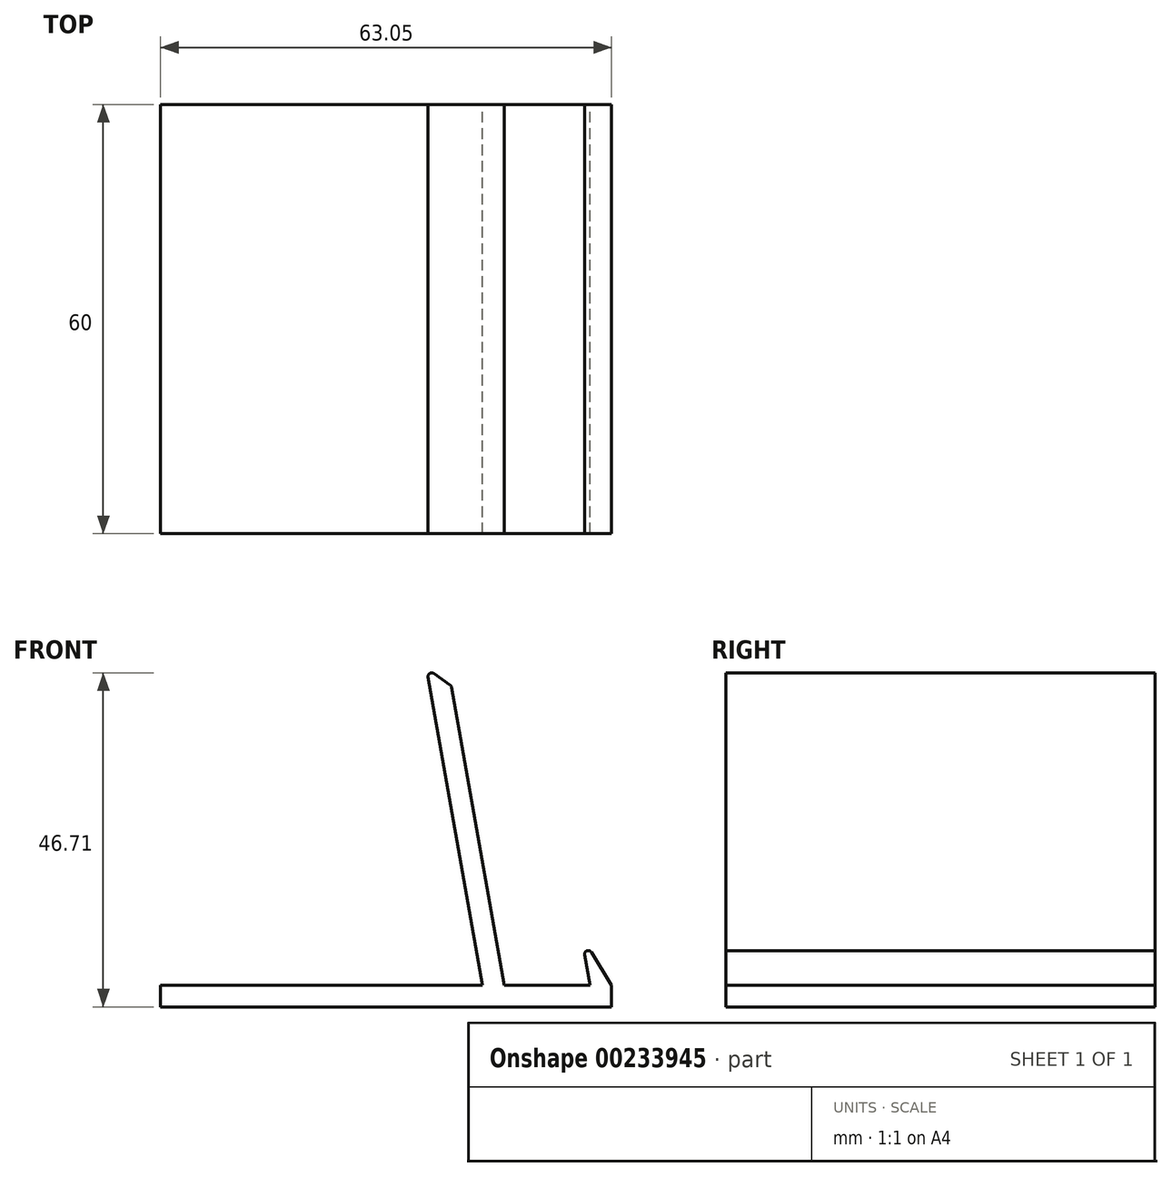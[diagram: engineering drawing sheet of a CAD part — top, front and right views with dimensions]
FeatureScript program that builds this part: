
annotation { "Feature Type Name" : "Feature", "Feature Type Description" : "" }
export const myFeature = defineFeature(function(context is Context, id is Id, definition is map)
    precondition{}
    {
        {
            var Q0;
            Q0=qCreatedBy(makeId("Front.planeOp"),FACE);
            var sketch = newSketch(context, id + "F0", { "sketchPlane" : qUnion([Q0])});
            skLineSegment(sketch, "E0", {"start": v(0, 0) * mm, "end": v(-63.05, 0) * mm});
            skLineSegment(sketch, "E1", {"start": v(-63.05, 0) * mm, "end": v(-63.05, 3) * mm});
            skLineSegment(sketch, "E2", {"start": v(-63.05, 3) * mm, "end": v(-18.05, 3) * mm});
            skLineSegment(sketch, "E3", {"start": v(-18.05, 3) * mm, "end": v(-25.86, 47.32) * mm});
            skLineSegment(sketch, "E4", {"start": v(-25.86, 47.32) * mm, "end": v(-22.39, 44.88) * mm});
            skLineSegment(sketch, "E5", {"start": v(-22.39, 44.88) * mm, "end": v(-15, 3) * mm});
            skLineSegment(sketch, "E6", {"start": v(-15, 3) * mm, "end": v(-3, 3) * mm});
            skLineSegment(sketch, "E7", {"start": v(-3, 3) * mm, "end": v(-4.22, 9.9) * mm});
            skLineSegment(sketch, "E8", {"start": v(-4.22, 9.9) * mm, "end": v(0, 3) * mm});
            skLineSegment(sketch, "E9", {"start": v(0, 3) * mm, "end": v(0, 0) * mm});
            skSolve(sketch);
        }
        {
            var Q0;
            Q0=makeQuery(id+"F0.imprint","IMPRINT",FACE,{"disambiguationData":[TD([[makeQuery(id+"F0.imprint","IMPRINT",EDGE,{"derivedFrom":sQuery(id+"F0.wireOp",EDGE,"E0")}),-1.0]])]});
            extrude(context, id + "F1", {"entities" : qUnion([Q0]), "endBound" : BoundingType.SYMMETRIC, "depth" : 60 * mm});
        }
        {
            var Q0;
            Q0=makeQuery(id+"F1.opExtrude","SWEPT_EDGE",EDGE,{"disambiguationData":[OSD([sQuery(id+"F0.wireOp",EDGE,"E4"),sQuery(id+"F0.wireOp",EDGE,"E5")])]});
            var Q1;
            Q1=makeQuery(id+"F1.opExtrude","SWEPT_EDGE",EDGE,{"disambiguationData":[OSD([sQuery(id+"F0.wireOp",EDGE,"E7"),sQuery(id+"F0.wireOp",EDGE,"E8")])]});
            var Q2;
            Q2=makeQuery(id+"F1.opExtrude","SWEPT_EDGE",EDGE,{"disambiguationData":[OSD([sQuery(id+"F0.wireOp",EDGE,"E3"),sQuery(id+"F0.wireOp",EDGE,"E4")])]});
            fillet(context, id + "F2", {"entities" : qUnion([Q0, Q1, Q2]), "radius" : .5 * mm, "tangentPropagation" : true, "allowEdgeOverflow" : false});
        }
    });
